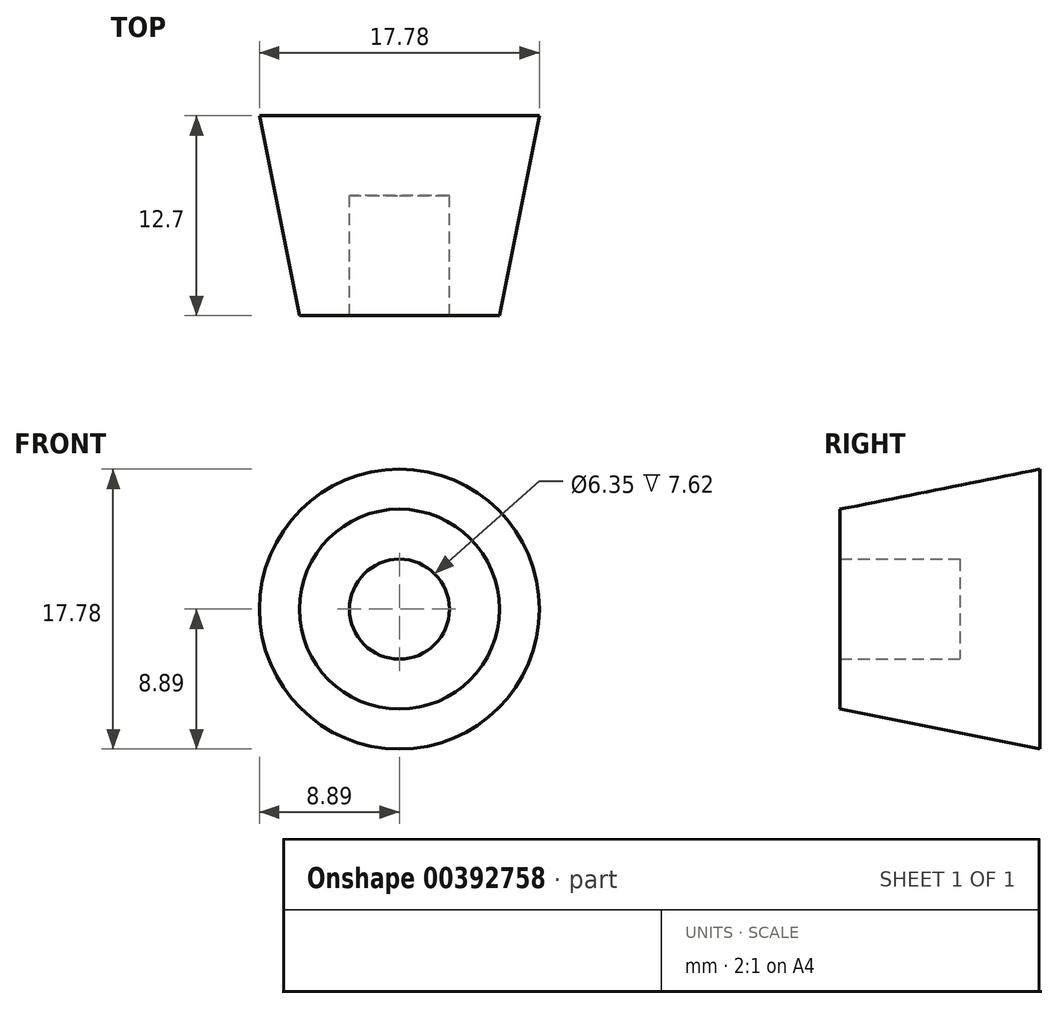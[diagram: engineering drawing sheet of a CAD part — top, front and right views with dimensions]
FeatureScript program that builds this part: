
annotation { "Feature Type Name" : "Feature", "Feature Type Description" : "" }
export const myFeature = defineFeature(function(context is Context, id is Id, definition is map)
    precondition{}
    {
        {
            var Q0;
            Q0=qCreatedBy(makeId("Top.planeOp"),FACE);
            var sketch = newSketch(context, id + "F0", { "sketchPlane" : qUnion([Q0])});
            skLineSegment(sketch, "E0", {"start": v(0, 15.24) * mm, "end": v(0, -12.06) * mm, "construction": true});
            skLineSegment(sketch, "E1", {"start": v(0, 13.18) * mm, "end": v(-8.9, 13.18) * mm});
            skLineSegment(sketch, "E2", {"start": v(-8.9, 13.18) * mm, "end": v(-6.35, 0.48) * mm});
            skLineSegment(sketch, "E3", {"start": v(-6.35, 0.48) * mm, "end": v(-3.18, 0.48) * mm});
            skLineSegment(sketch, "E4", {"start": v(-3.18, 0.48) * mm, "end": v(-3.18, 8.1) * mm});
            skLineSegment(sketch, "E5", {"start": v(-3.18, 8.1) * mm, "end": v(0, 8.1) * mm});
            skLineSegment(sketch, "E6", {"start": v(0, 8.1) * mm, "end": v(0, 13.18) * mm});
            skSolve(sketch);
        }
        {
            var Q0;
            Q0=makeQuery(id+"F0.imprint","IMPRINT",FACE,{"disambiguationData":[TD([[makeQuery(id+"F0.imprint","IMPRINT",EDGE,{"derivedFrom":sQuery(id+"F0.wireOp",EDGE,"E1")}),1.0]])]});
            var Q1;
            Q1=sQuery(id+"F0.wireOp",EDGE,"E0");
            revolve(context, id + "F1", {"entities" : qUnion([Q0]), "axis" : qUnion([Q1]), "revolveType" : RevolveType.FULL});
        }
    });
